# Revit family: Thorn CESAR AMP WALL
name_source: partatom
category: Lighting Fixtures
units: mm (PartAtom-declared; Revit-internal decimal feet)

## family parameters
Cut with Voids When Loaded = Yes
Host = Face
Light Source = No
Maintain Annotation Orientation = No
Part Type = Normal
Room Calculation Point = Yes
Round Connector Dimension = Use Diameter
Shared = No

## types (120) — shared parameters
Assembly Code = Pr_70_70_48_17
Default Elevation = 1000 mm  [stored 3.28084 ft]
Description = Outdoor Wall Mounted Luminaire
Export Type to IFC As = IfcLightFixtureType
Lamp = LED
Manufacturer = Thorn Lighting
Power Factor = 1
R = 36 mm  [stored 0.11811 ft]
Type IFC Predefined Type = DIRECTIONSOURCE
URL = https://www.thornlighting.com

## per-type parameters (varying)
| type | Apparent Load | D | E | Housing L | Housing M | Housing S | Luminaire Height | Luminaire Length | Luminaire Width | Material | Model | Type Image | Type Light Source Down | Type Light Source Up | Up and Down | Wattage |
| CESAR AMP S DWN 1 L927 WB RD WH | 9 VA | 45 mm  [stored 0.147638 ft] | 12 mm  [stored 0.0393701 ft] | No | No | Yes | 250 mm  [stored 0.82021 ft] | 145 mm  [stored 0.475722 ft] | 90 mm  [stored 0.295276 ft] | Thorn-Aluminium-RAL 9016-Traffic White | 96701186 | TLG_CESA_F_AMP_DWN_WB_WH.jpg | Thorn-Light Source-Cesar-Amp-Wall : CESAR AMP S DWN 1 L927 WB RD WH_photometric_data | Thorn-Light Source-Cesar-Amp-Wall : CESAR AMP S DWN 1 L927 WB RD WH_photometric_data | No | 9 W |
| CESAR AMP S DWN 1L927WB HF ANT | 9 VA | 45 mm  [stored 0.147638 ft] | 12 mm  [stored 0.0393701 ft] | No | No | Yes | 250 mm  [stored 0.82021 ft] | 145 mm  [stored 0.475722 ft] | 90 mm  [stored 0.295276 ft] | Thorn-Aluminium-RAL 7016-Anthracite Grey | 96700037 | TLG_CESA_F_AMP_DWN_WB_ANT.jpg | Thorn-Light Source-Cesar-Amp-Wall : CESAR AMP S DWN 1L927WB HF ANT_photometric_data | Thorn-Light Source-Cesar-Amp-Wall : CESAR AMP S DWN 1L927WB HF ANT_photometric_data | No | 9 W |
| CESAR AMP S DWN 1L927WB HF BK | 9 VA | 45 mm  [stored 0.147638 ft] | 12 mm  [stored 0.0393701 ft] | No | No | Yes | 250 mm  [stored 0.82021 ft] | 145 mm  [stored 0.475722 ft] | 90 mm  [stored 0.295276 ft] | Thorn-Aluminium-RAL 9005-Jet Black | 96700035 | TLG_CESA_F_AMP_DWN_WB_BK.jpg | Thorn-Light Source-Cesar-Amp-Wall : CESAR AMP S DWN 1L927WB HF BK_photometric_data | Thorn-Light Source-Cesar-Amp-Wall : CESAR AMP S DWN 1L927WB HF BK_photometric_data | No | 9 W |
| CESAR AMP S DWN 1L927WB HF GY | 9 VA | 45 mm  [stored 0.147638 ft] | 12 mm  [stored 0.0393701 ft] | No | No | Yes | 250 mm  [stored 0.82021 ft] | 145 mm  [stored 0.475722 ft] | 90 mm  [stored 0.295276 ft] | Thorn-Aluminium-RAL 9006-White Aluminium | 96700036 | TLG_CESA_F_AMP_DWN_WB_GY.jpg | Thorn-Light Source-Cesar-Amp-Wall : CESAR AMP S DWN 1L927WB HF GY_photometric_data | Thorn-Light Source-Cesar-Amp-Wall : CESAR AMP S DWN 1L927WB HF GY_photometric_data | No | 9 W |
| CESAR AMP S DWN 1L927WB RD ANT | 9 VA | 45 mm  [stored 0.147638 ft] | 12 mm  [stored 0.0393701 ft] | No | No | Yes | 250 mm  [stored 0.82021 ft] | 145 mm  [stored 0.475722 ft] | 90 mm  [stored 0.295276 ft] | Thorn-Aluminium-RAL 7016-Anthracite Grey | 96701189 | TLG_CESA_F_AMP_DWN_WB_ANT_DarkSkyApproved.jpg | Thorn-Light Source-Cesar-Amp-Wall : CESAR AMP S DWN 1L927WB RD ANT_photometric_data | Thorn-Light Source-Cesar-Amp-Wall : CESAR AMP S DWN 1L927WB RD ANT_photometric_data | No | 9 W |
| CESAR AMP S DWN 1L927WB RD BK | 9 VA | 45 mm  [stored 0.147638 ft] | 12 mm  [stored 0.0393701 ft] | No | No | Yes | 250 mm  [stored 0.82021 ft] | 145 mm  [stored 0.475722 ft] | 90 mm  [stored 0.295276 ft] | Thorn-Aluminium-RAL 9005-Jet Black | 96701187 | TLG_CESA_F_AMP_DWN_WB_BK.jpg | Thorn-Light Source-Cesar-Amp-Wall : CESAR AMP S DWN 1L927WB RD BK_photometric_data | Thorn-Light Source-Cesar-Amp-Wall : CESAR AMP S DWN 1L927WB RD BK_photometric_data | No | 9 W |
| CESAR AMP S DWN 1L927WB RD GY | 9 VA | 45 mm  [stored 0.147638 ft] | 12 mm  [stored 0.0393701 ft] | No | No | Yes | 250 mm  [stored 0.82021 ft] | 145 mm  [stored 0.475722 ft] | 90 mm  [stored 0.295276 ft] | Thorn-Aluminium-RAL 9006-White Aluminium | 96701188 | TLG_CESA_F_AMP_DWN_WB_GY.jpg | Thorn-Light Source-Cesar-Amp-Wall : CESAR AMP S DWN 1L927WB RD GY_photometric_data | Thorn-Light Source-Cesar-Amp-Wall : CESAR AMP S DWN 1L927WB RD GY_photometric_data | No | 9 W |
| CESAR AMP S DWN 1L927WBHF WH | 9 VA | 45 mm  [stored 0.147638 ft] | 12 mm  [stored 0.0393701 ft] | No | No | Yes | 250 mm  [stored 0.82021 ft] | 145 mm  [stored 0.475722 ft] | 90 mm  [stored 0.295276 ft] | Thorn-Aluminium-RAL 9016-Traffic White | 96700034 | TLG_CESA_F_AMP_DWN_WB_WH.jpg | Thorn-Light Source-Cesar-Amp-Wall : CESAR AMP S DWN 1L927WBHF WH_photometric_data | Thorn-Light Source-Cesar-Amp-Wall : CESAR AMP S DWN 1L927WBHF WH_photometric_data | No | 9 W |
| CESAR AMP S DWN 1L930WB HF ANT | 9 VA | 45 mm  [stored 0.147638 ft] | 12 mm  [stored 0.0393701 ft] | No | No | Yes | 250 mm  [stored 0.82021 ft] | 145 mm  [stored 0.475722 ft] | 90 mm  [stored 0.295276 ft] | Thorn-Aluminium-RAL 7016-Anthracite Grey | 96700045 | TLG_CESA_F_AMP_DWN_WB_ANT.jpg | Thorn-Light Source-Cesar-Amp-Wall : CESAR AMP S DWN 1L930WB HF ANT_photometric_data | Thorn-Light Source-Cesar-Amp-Wall : CESAR AMP S DWN 1L930WB HF ANT_photometric_data | No | 9 W |
| CESAR AMP S DWN 1L930WB HF BK | 9 VA | 45 mm  [stored 0.147638 ft] | 12 mm  [stored 0.0393701 ft] | No | No | Yes | 250 mm  [stored 0.82021 ft] | 145 mm  [stored 0.475722 ft] | 90 mm  [stored 0.295276 ft] | Thorn-Aluminium-RAL 9005-Jet Black | 96700043 | TLG_CESA_F_AMP_DWN_WB_BK.jpg | Thorn-Light Source-Cesar-Amp-Wall : CESAR AMP S DWN 1L930WB HF BK_photometric_data | Thorn-Light Source-Cesar-Amp-Wall : CESAR AMP S DWN 1L930WB HF BK_photometric_data | No | 9 W |
| CESAR AMP S DWN 1L930WB HF GY | 9 VA | 45 mm  [stored 0.147638 ft] | 12 mm  [stored 0.0393701 ft] | No | No | Yes | 250 mm  [stored 0.82021 ft] | 145 mm  [stored 0.475722 ft] | 90 mm  [stored 0.295276 ft] | Thorn-Aluminium-RAL 9006-White Aluminium | 96700044 | TLG_CESA_F_AMP_DWN_WB_GY.jpg | Thorn-Light Source-Cesar-Amp-Wall : CESAR AMP S DWN 1L930WB HF GY_photometric_data | Thorn-Light Source-Cesar-Amp-Wall : CESAR AMP S DWN 1L930WB HF GY_photometric_data | No | 9 W |
| CESAR AMP S DWN 1L930WB HF WH | 9 VA | 45 mm  [stored 0.147638 ft] | 12 mm  [stored 0.0393701 ft] | No | No | Yes | 250 mm  [stored 0.82021 ft] | 145 mm  [stored 0.475722 ft] | 90 mm  [stored 0.295276 ft] | Thorn-Aluminium-RAL 9016-Traffic White | 96700042 | TLG_CESA_F_AMP_DWN_WB_WH.jpg | Thorn-Light Source-Cesar-Amp-Wall : CESAR AMP S DWN 1L930WB HF WH_photometric_data | Thorn-Light Source-Cesar-Amp-Wall : CESAR AMP S DWN 1L930WB HF WH_photometric_data | No | 9 W |
| CESAR AMP S DWN 1L930WB RD ANT | 9 VA | 45 mm  [stored 0.147638 ft] | 12 mm  [stored 0.0393701 ft] | No | No | Yes | 250 mm  [stored 0.82021 ft] | 145 mm  [stored 0.475722 ft] | 90 mm  [stored 0.295276 ft] | Thorn-Aluminium-RAL 7016-Anthracite Grey | 96701197 | TLG_CESA_F_AMP_DWN_WB_ANT_DarkSkyApproved.jpg | Thorn-Light Source-Cesar-Amp-Wall : CESAR AMP S DWN 1L930WB RD ANT_photometric_data | Thorn-Light Source-Cesar-Amp-Wall : CESAR AMP S DWN 1L930WB RD ANT_photometric_data | No | 9 W |
| CESAR AMP S DWN 1L930WB RD BK | 9 VA | 45 mm  [stored 0.147638 ft] | 12 mm  [stored 0.0393701 ft] | No | No | Yes | 250 mm  [stored 0.82021 ft] | 145 mm  [stored 0.475722 ft] | 90 mm  [stored 0.295276 ft] | Thorn-Aluminium-RAL 9005-Jet Black | 96701195 | TLG_CESA_F_AMP_DWN_WB_BK.jpg | Thorn-Light Source-Cesar-Amp-Wall : CESAR AMP S DWN 1L930WB RD BK_photometric_data | Thorn-Light Source-Cesar-Amp-Wall : CESAR AMP S DWN 1L930WB RD BK_photometric_data | No | 9 W |
| CESAR AMP S DWN 1L930WB RD GY | 9 VA | 45 mm  [stored 0.147638 ft] | 12 mm  [stored 0.0393701 ft] | No | No | Yes | 250 mm  [stored 0.82021 ft] | 145 mm  [stored 0.475722 ft] | 90 mm  [stored 0.295276 ft] | Thorn-Aluminium-RAL 9006-White Aluminium | 96701196 | TLG_CESA_F_AMP_DWN_WB_GY.jpg | Thorn-Light Source-Cesar-Amp-Wall : CESAR AMP S DWN 1L930WB RD GY_photometric_data | Thorn-Light Source-Cesar-Amp-Wall : CESAR AMP S DWN 1L930WB RD GY_photometric_data | No | 9 W |
| CESAR AMP S DWN 1L930WB RD WH | 9 VA | 45 mm  [stored 0.147638 ft] | 12 mm  [stored 0.0393701 ft] | No | No | Yes | 250 mm  [stored 0.82021 ft] | 145 mm  [stored 0.475722 ft] | 90 mm  [stored 0.295276 ft] | Thorn-Aluminium-RAL 9016-Traffic White | 96701194 | TLG_CESA_F_AMP_DWN_WB_WH.jpg | Thorn-Light Source-Cesar-Amp-Wall : CESAR AMP S DWN 1L930WB RD WH_photometric_data | Thorn-Light Source-Cesar-Amp-Wall : CESAR AMP S DWN 1L930WB RD WH_photometric_data | No | 9 W |
| CESAR AMP S DWN 1L940WB HF ANT | 9 VA | 45 mm  [stored 0.147638 ft] | 12 mm  [stored 0.0393701 ft] | No | No | Yes | 250 mm  [stored 0.82021 ft] | 145 mm  [stored 0.475722 ft] | 90 mm  [stored 0.295276 ft] | Thorn-Aluminium-RAL 7016-Anthracite Grey | 96700041 | TLG_CESA_F_AMP_DWN_WB_ANT.jpg | Thorn-Light Source-Cesar-Amp-Wall : CESAR AMP S DWN 1L940WB HF ANT_photometric_data | Thorn-Light Source-Cesar-Amp-Wall : CESAR AMP S DWN 1L940WB HF ANT_photometric_data | No | 9 W |
| CESAR AMP S DWN 1L940WB HF BK | 9 VA | 45 mm  [stored 0.147638 ft] | 12 mm  [stored 0.0393701 ft] | No | No | Yes | 250 mm  [stored 0.82021 ft] | 145 mm  [stored 0.475722 ft] | 90 mm  [stored 0.295276 ft] | Thorn-Aluminium-RAL 9005-Jet Black | 96700039 | TLG_CESA_F_AMP_DWN_WB_BK.jpg | Thorn-Light Source-Cesar-Amp-Wall : CESAR AMP S DWN 1L940WB HF BK_photometric_data | Thorn-Light Source-Cesar-Amp-Wall : CESAR AMP S DWN 1L940WB HF BK_photometric_data | No | 9 W |
| CESAR AMP S DWN 1L940WB HF GY | 9 VA | 45 mm  [stored 0.147638 ft] | 12 mm  [stored 0.0393701 ft] | No | No | Yes | 250 mm  [stored 0.82021 ft] | 145 mm  [stored 0.475722 ft] | 90 mm  [stored 0.295276 ft] | Thorn-Aluminium-RAL 9006-White Aluminium | 96700040 | TLG_CESA_F_AMP_DWN_WB_GY.jpg | Thorn-Light Source-Cesar-Amp-Wall : CESAR AMP S DWN 1L940WB HF GY_photometric_data | Thorn-Light Source-Cesar-Amp-Wall : CESAR AMP S DWN 1L940WB HF GY_photometric_data | No | 9 W |
| CESAR AMP S DWN 1L940WB HF WH | 9 VA | 45 mm  [stored 0.147638 ft] | 12 mm  [stored 0.0393701 ft] | No | No | Yes | 250 mm  [stored 0.82021 ft] | 145 mm  [stored 0.475722 ft] | 90 mm  [stored 0.295276 ft] | Thorn-Aluminium-RAL 9016-Traffic White | 96700038 | TLG_CESA_F_AMP_DWN_WB_WH.jpg | Thorn-Light Source-Cesar-Amp-Wall : CESAR AMP S DWN 1L940WB HF WH_photometric_data | Thorn-Light Source-Cesar-Amp-Wall : CESAR AMP S DWN 1L940WB HF WH_photometric_data | No | 9 W |
| CESAR AMP S DWN 1L940WB RD ANT | 9 VA | 45 mm  [stored 0.147638 ft] | 12 mm  [stored 0.0393701 ft] | No | No | Yes | 250 mm  [stored 0.82021 ft] | 145 mm  [stored 0.475722 ft] | 90 mm  [stored 0.295276 ft] | Thorn-Aluminium-RAL 7016-Anthracite Grey | 96701193 | TLG_CESA_F_AMP_DWN_WB_ANT.jpg | Thorn-Light Source-Cesar-Amp-Wall : CESAR AMP S DWN 1L940WB RD ANT_photometric_data | Thorn-Light Source-Cesar-Amp-Wall : CESAR AMP S DWN 1L940WB RD ANT_photometric_data | No | 9 W |
| CESAR AMP S DWN 1L940WB RD BK | 9 VA | 45 mm  [stored 0.147638 ft] | 12 mm  [stored 0.0393701 ft] | No | No | Yes | 250 mm  [stored 0.82021 ft] | 145 mm  [stored 0.475722 ft] | 90 mm  [stored 0.295276 ft] | Thorn-Aluminium-RAL 9005-Jet Black | 96701191 | TLG_CESA_F_AMP_DWN_WB_BK.jpg | Thorn-Light Source-Cesar-Amp-Wall : CESAR AMP S DWN 1L940WB RD BK_photometric_data | Thorn-Light Source-Cesar-Amp-Wall : CESAR AMP S DWN 1L940WB RD BK_photometric_data | No | 9 W |
| CESAR AMP S DWN 1L940WB RD GY | 9 VA | 45 mm  [stored 0.147638 ft] | 12 mm  [stored 0.0393701 ft] | No | No | Yes | 250 mm  [stored 0.82021 ft] | 145 mm  [stored 0.475722 ft] | 90 mm  [stored 0.295276 ft] | Thorn-Aluminium-RAL 9006-White Aluminium | 96701192 | TLG_CESA_F_AMP_DWN_WB_GY.jpg | Thorn-Light Source-Cesar-Amp-Wall : CESAR AMP S DWN 1L940WB RD GY_photometric_data | Thorn-Light Source-Cesar-Amp-Wall : CESAR AMP S DWN 1L940WB RD GY_photometric_data | No | 9 W |
| CESAR AMP S DWN 1L940WB RD WH | 9 VA | 45 mm  [stored 0.147638 ft] | 12 mm  [stored 0.0393701 ft] | No | No | Yes | 250 mm  [stored 0.82021 ft] | 145 mm  [stored 0.475722 ft] | 90 mm  [stored 0.295276 ft] | Thorn-Aluminium-RAL 9016-Traffic White | 96701190 | TLG_CESA_F_AMP_DWN_WB_WH.jpg | Thorn-Light Source-Cesar-Amp-Wall : CESAR AMP S DWN 1L940WB RD WH_photometric_data | Thorn-Light Source-Cesar-Amp-Wall : CESAR AMP S DWN 1L940WB RD WH_photometric_data | No | 9 W |
| CESAR AMP S U/D 2L927WB HF ANT | 15 VA | 45 mm  [stored 0.147638 ft] | 12 mm  [stored 0.0393701 ft] | No | No | Yes | 250 mm  [stored 0.82021 ft] | 145 mm  [stored 0.475722 ft] | 90 mm  [stored 0.295276 ft] | Thorn-Aluminium-RAL 7016-Anthracite Grey | 96700049 | TLG_CESA_F_AMP_UD_WB_ANT.jpg | Thorn-Light Source-Cesar-Amp-Wall : CESAR AMP S U/D 2L927WB HF ANT_photometric_data_DOWN | Thorn-Light Source-Cesar-Amp-Wall : CESAR AMP S U/D 2L927WB HF ANT_photometric_data_UP | Yes | 15 W |
| CESAR AMP S U/D 2L927WB HF BK | 15 VA | 45 mm  [stored 0.147638 ft] | 12 mm  [stored 0.0393701 ft] | No | No | Yes | 250 mm  [stored 0.82021 ft] | 145 mm  [stored 0.475722 ft] | 90 mm  [stored 0.295276 ft] | Thorn-Aluminium-RAL 9005-Jet Black | 96700047 | TLG_CESA_F_AMP_UD_WB_BK.jpg | Thorn-Light Source-Cesar-Amp-Wall : CESAR AMP S U/D 2L927WB HF BK_photometric_data_DOWN | Thorn-Light Source-Cesar-Amp-Wall : CESAR AMP S U/D 2L927WB HF BK_photometric_data_UP | Yes | 15 W |
| CESAR AMP S U/D 2L927WB HF GY | 15 VA | 45 mm  [stored 0.147638 ft] | 12 mm  [stored 0.0393701 ft] | No | No | Yes | 250 mm  [stored 0.82021 ft] | 145 mm  [stored 0.475722 ft] | 90 mm  [stored 0.295276 ft] | Thorn-Aluminium-RAL 9006-White Aluminium | 96700048 | TLG_CESA_F_AMP_UD_WB_GY.jpg | Thorn-Light Source-Cesar-Amp-Wall : CESAR AMP S U/D 2L927WB HF GY_photometric_data_DOWN | Thorn-Light Source-Cesar-Amp-Wall : CESAR AMP S U/D 2L927WB HF GY_photometric_data_UP | Yes | 15 W |
| CESAR AMP S U/D 2L927WB HF WH | 15 VA | 45 mm  [stored 0.147638 ft] | 12 mm  [stored 0.0393701 ft] | No | No | Yes | 250 mm  [stored 0.82021 ft] | 145 mm  [stored 0.475722 ft] | 90 mm  [stored 0.295276 ft] | Thorn-Aluminium-RAL 9016-Traffic White | 96700046 | TLG_CESA_F_AMP_UD_WB_WH.jpg | Thorn-Light Source-Cesar-Amp-Wall : CESAR AMP S U/D 2L927WB HF WH_photometric_data_DOWN | Thorn-Light Source-Cesar-Amp-Wall : CESAR AMP S U/D 2L927WB HF WH_photometric_data_UP | Yes | 15 W |
| CESAR AMP S U/D 2L927WB RD ANT | 15 VA | 45 mm  [stored 0.147638 ft] | 12 mm  [stored 0.0393701 ft] | No | No | Yes | 250 mm  [stored 0.82021 ft] | 145 mm  [stored 0.475722 ft] | 90 mm  [stored 0.295276 ft] | Thorn-Aluminium-RAL 7016-Anthracite Grey | 96701201 | TLG_CESA_F_AMP_UD_WB_ANT.jpg | Thorn-Light Source-Cesar-Amp-Wall : CESAR AMP S U/D 2L927WB RD ANT_photometric_data_DOWN | Thorn-Light Source-Cesar-Amp-Wall : CESAR AMP S U/D 2L927WB RD ANT_photometric_data_UP | Yes | 15 W |
| CESAR AMP S U/D 2L927WB RD BK | 15 VA | 45 mm  [stored 0.147638 ft] | 12 mm  [stored 0.0393701 ft] | No | No | Yes | 250 mm  [stored 0.82021 ft] | 145 mm  [stored 0.475722 ft] | 90 mm  [stored 0.295276 ft] | Thorn-Aluminium-RAL 9005-Jet Black | 96701199 | TLG_CESA_F_AMP_UD_WB_BK.jpg | Thorn-Light Source-Cesar-Amp-Wall : CESAR AMP S U/D 2L927WB RD BK_photometric_data_DOWN | Thorn-Light Source-Cesar-Amp-Wall : CESAR AMP S U/D 2L927WB RD BK_photometric_data_UP | Yes | 15 W |
| CESAR AMP S U/D 2L927WB RD GY | 15 VA | 45 mm  [stored 0.147638 ft] | 12 mm  [stored 0.0393701 ft] | No | No | Yes | 250 mm  [stored 0.82021 ft] | 145 mm  [stored 0.475722 ft] | 90 mm  [stored 0.295276 ft] | Thorn-Aluminium-RAL 9006-White Aluminium | 96701200 | TLG_CESA_F_AMP_UD_WB_GY.jpg | Thorn-Light Source-Cesar-Amp-Wall : CESAR AMP S U/D 2L927WB RD GY_photometric_data_DOWN | Thorn-Light Source-Cesar-Amp-Wall : CESAR AMP S U/D 2L927WB RD GY_photometric_data_UP | Yes | 15 W |
| CESAR AMP S U/D 2L927WB RD WH | 15 VA | 45 mm  [stored 0.147638 ft] | 12 mm  [stored 0.0393701 ft] | No | No | Yes | 250 mm  [stored 0.82021 ft] | 145 mm  [stored 0.475722 ft] | 90 mm  [stored 0.295276 ft] | Thorn-Aluminium-RAL 9016-Traffic White | 96701198 | TLG_CESA_F_AMP_UD_WB_WH.jpg | Thorn-Light Source-Cesar-Amp-Wall : CESAR AMP S U/D 2L927WB RD WH_photometric_data_DOWN | Thorn-Light Source-Cesar-Amp-Wall : CESAR AMP S U/D 2L927WB RD WH_photometric_data_UP | Yes | 15 W |
| CESAR AMP S U/D 2L930WB HF ANT | 15 VA | 45 mm  [stored 0.147638 ft] | 12 mm  [stored 0.0393701 ft] | No | No | Yes | 250 mm  [stored 0.82021 ft] | 145 mm  [stored 0.475722 ft] | 90 mm  [stored 0.295276 ft] | Thorn-Aluminium-RAL 7016-Anthracite Grey | 96700057 | TLG_CESA_F_AMP_UD_WB_ANT.jpg | Thorn-Light Source-Cesar-Amp-Wall : CESAR AMP S U/D 2L930WB HF ANT_photometric_data_DOWN | Thorn-Light Source-Cesar-Amp-Wall : CESAR AMP S U/D 2L930WB HF ANT_photometric_data_UP | Yes | 15 W |
| CESAR AMP S U/D 2L930WB HF BK | 15 VA | 45 mm  [stored 0.147638 ft] | 12 mm  [stored 0.0393701 ft] | No | No | Yes | 250 mm  [stored 0.82021 ft] | 145 mm  [stored 0.475722 ft] | 90 mm  [stored 0.295276 ft] | Thorn-Aluminium-RAL 9005-Jet Black | 96700055 | TLG_CESA_F_AMP_UD_WB_BK.jpg | Thorn-Light Source-Cesar-Amp-Wall : CESAR AMP S U/D 2L930WB HF BK_photometric_data_DOWN | Thorn-Light Source-Cesar-Amp-Wall : CESAR AMP S U/D 2L930WB HF BK_photometric_data_UP | Yes | 15 W |
| CESAR AMP S U/D 2L930WB HF GY | 15 VA | 45 mm  [stored 0.147638 ft] | 12 mm  [stored 0.0393701 ft] | No | No | Yes | 250 mm  [stored 0.82021 ft] | 145 mm  [stored 0.475722 ft] | 90 mm  [stored 0.295276 ft] | Thorn-Aluminium-RAL 9006-White Aluminium | 96700056 | TLG_CESA_F_AMP_UD_WB_GY.jpg | Thorn-Light Source-Cesar-Amp-Wall : CESAR AMP S U/D 2L930WB HF GY_photometric_data_DOWN | Thorn-Light Source-Cesar-Amp-Wall : CESAR AMP S U/D 2L930WB HF GY_photometric_data_UP | Yes | 15 W |
| CESAR AMP S U/D 2L930WB HF WH | 15 VA | 45 mm  [stored 0.147638 ft] | 12 mm  [stored 0.0393701 ft] | No | No | Yes | 250 mm  [stored 0.82021 ft] | 145 mm  [stored 0.475722 ft] | 90 mm  [stored 0.295276 ft] | Thorn-Aluminium-RAL 9016-Traffic White | 96700054 | TLG_CESA_F_AMP_UD_WB_WH.jpg | Thorn-Light Source-Cesar-Amp-Wall : CESAR AMP S U/D 2L930WB HF WH_photometric_data_DOWN | Thorn-Light Source-Cesar-Amp-Wall : CESAR AMP S U/D 2L930WB HF WH_photometric_data_UP | Yes | 15 W |
| CESAR AMP S U/D 2L930WB RD ANT | 15 VA | 45 mm  [stored 0.147638 ft] | 12 mm  [stored 0.0393701 ft] | No | No | Yes | 250 mm  [stored 0.82021 ft] | 145 mm  [stored 0.475722 ft] | 90 mm  [stored 0.295276 ft] | Thorn-Aluminium-RAL 7016-Anthracite Grey | 96701209 | TLG_CESA_F_AMP_UD_WB_ANT.jpg | Thorn-Light Source-Cesar-Amp-Wall : CESAR AMP S U/D 2L930WB RD ANT_photometric_data_DOWN | Thorn-Light Source-Cesar-Amp-Wall : CESAR AMP S U/D 2L930WB RD ANT_photometric_data_UP | Yes | 15 W |
| CESAR AMP S U/D 2L930WB RD BK | 15 VA | 45 mm  [stored 0.147638 ft] | 12 mm  [stored 0.0393701 ft] | No | No | Yes | 250 mm  [stored 0.82021 ft] | 145 mm  [stored 0.475722 ft] | 90 mm  [stored 0.295276 ft] | Thorn-Aluminium-RAL 9005-Jet Black | 96701207 | TLG_CESA_F_AMP_UD_WB_BK.jpg | Thorn-Light Source-Cesar-Amp-Wall : CESAR AMP S U/D 2L930WB RD BK_photometric_data_DOWN | Thorn-Light Source-Cesar-Amp-Wall : CESAR AMP S U/D 2L930WB RD BK_photometric_data_UP | Yes | 15 W |
| CESAR AMP S U/D 2L930WB RD GY | 15 VA | 45 mm  [stored 0.147638 ft] | 12 mm  [stored 0.0393701 ft] | No | No | Yes | 250 mm  [stored 0.82021 ft] | 145 mm  [stored 0.475722 ft] | 90 mm  [stored 0.295276 ft] | Thorn-Aluminium-RAL 9006-White Aluminium | 96701208 | TLG_CESA_F_AMP_UD_WB_GY.jpg | Thorn-Light Source-Cesar-Amp-Wall : CESAR AMP S U/D 2L930WB RD GY_photometric_data_DOWN | Thorn-Light Source-Cesar-Amp-Wall : CESAR AMP S U/D 2L930WB RD GY_photometric_data_UP | Yes | 15 W |
| CESAR AMP S U/D 2L930WB RD WH | 15 VA | 45 mm  [stored 0.147638 ft] | 12 mm  [stored 0.0393701 ft] | No | No | Yes | 250 mm  [stored 0.82021 ft] | 145 mm  [stored 0.475722 ft] | 90 mm  [stored 0.295276 ft] | Thorn-Aluminium-RAL 9016-Traffic White | 96701206 | TLG_CESA_F_AMP_UD_WB_WH.jpg | Thorn-Light Source-Cesar-Amp-Wall : CESAR AMP S U/D 2L930WB RD WH_photometric_data_DOWN | Thorn-Light Source-Cesar-Amp-Wall : CESAR AMP S U/D 2L930WB RD WH_photometric_data_UP | Yes | 15 W |
| CESAR AMP S U/D 2L940WB HF ANT | 15 VA | 45 mm  [stored 0.147638 ft] | 12 mm  [stored 0.0393701 ft] | No | No | Yes | 250 mm  [stored 0.82021 ft] | 145 mm  [stored 0.475722 ft] | 90 mm  [stored 0.295276 ft] | Thorn-Aluminium-RAL 7016-Anthracite Grey | 96700053 | TLG_CESA_F_AMP_UD_WB_ANT.jpg | Thorn-Light Source-Cesar-Amp-Wall : CESAR AMP S U/D 2L940WB HF ANT_photometric_data_DOWN | Thorn-Light Source-Cesar-Amp-Wall : CESAR AMP S U/D 2L940WB HF ANT_photometric_data_UP | Yes | 15 W |
| CESAR AMP S U/D 2L940WB HF BK | 15 VA | 45 mm  [stored 0.147638 ft] | 12 mm  [stored 0.0393701 ft] | No | No | Yes | 250 mm  [stored 0.82021 ft] | 145 mm  [stored 0.475722 ft] | 90 mm  [stored 0.295276 ft] | Thorn-Aluminium-RAL 9005-Jet Black | 96700051 | TLG_CESA_F_AMP_UD_WB_BK.jpg | Thorn-Light Source-Cesar-Amp-Wall : CESAR AMP S U/D 2L940WB HF BK_photometric_data_DOWN | Thorn-Light Source-Cesar-Amp-Wall : CESAR AMP S U/D 2L940WB HF BK_photometric_data_UP | Yes | 15 W |
| CESAR AMP S U/D 2L940WB HF GY | 15 VA | 45 mm  [stored 0.147638 ft] | 12 mm  [stored 0.0393701 ft] | No | No | Yes | 250 mm  [stored 0.82021 ft] | 145 mm  [stored 0.475722 ft] | 90 mm  [stored 0.295276 ft] | Thorn-Aluminium-RAL 9006-White Aluminium | 96700052 | TLG_CESA_F_AMP_UD_WB_GY.jpg | Thorn-Light Source-Cesar-Amp-Wall : CESAR AMP S U/D 2L940WB HF GY_photometric_data_DOWN | Thorn-Light Source-Cesar-Amp-Wall : CESAR AMP S U/D 2L940WB HF GY_photometric_data_UP | Yes | 15 W |
| CESAR AMP S U/D 2L940WB HF WH | 15 VA | 45 mm  [stored 0.147638 ft] | 12 mm  [stored 0.0393701 ft] | No | No | Yes | 250 mm  [stored 0.82021 ft] | 145 mm  [stored 0.475722 ft] | 90 mm  [stored 0.295276 ft] | Thorn-Aluminium-RAL 9016-Traffic White | 96700050 | TLG_CESA_F_AMP_UD_WB_WH.jpg | Thorn-Light Source-Cesar-Amp-Wall : CESAR AMP S U/D 2L940WB HF WH_photometric_data_DOWN | Thorn-Light Source-Cesar-Amp-Wall : CESAR AMP S U/D 2L940WB HF WH_photometric_data_UP | Yes | 15 W |
| CESAR AMP S U/D 2L940WB RD ANT | 15 VA | 45 mm  [stored 0.147638 ft] | 12 mm  [stored 0.0393701 ft] | No | No | Yes | 250 mm  [stored 0.82021 ft] | 145 mm  [stored 0.475722 ft] | 90 mm  [stored 0.295276 ft] | Thorn-Aluminium-RAL 7016-Anthracite Grey | 96701205 | TLG_CESA_F_AMP_UD_WB_ANT.jpg | Thorn-Light Source-Cesar-Amp-Wall : CESAR AMP S U/D 2L940WB RD ANT_photometric_data_DOWN | Thorn-Light Source-Cesar-Amp-Wall : CESAR AMP S U/D 2L940WB RD ANT_photometric_data_UP | Yes | 15 W |
| CESAR AMP S U/D 2L940WB RD BK | 15 VA | 45 mm  [stored 0.147638 ft] | 12 mm  [stored 0.0393701 ft] | No | No | Yes | 250 mm  [stored 0.82021 ft] | 145 mm  [stored 0.475722 ft] | 90 mm  [stored 0.295276 ft] | Thorn-Aluminium-RAL 9005-Jet Black | 96701203 | TLG_CESA_F_AMP_UD_WB_BK.jpg | Thorn-Light Source-Cesar-Amp-Wall : CESAR AMP S U/D 2L940WB RD BK_photometric_data_DOWN | Thorn-Light Source-Cesar-Amp-Wall : CESAR AMP S U/D 2L940WB RD BK_photometric_data_UP | Yes | 15 W |
| CESAR AMP S U/D 2L940WB RD GY | 15 VA | 45 mm  [stored 0.147638 ft] | 12 mm  [stored 0.0393701 ft] | No | No | Yes | 250 mm  [stored 0.82021 ft] | 145 mm  [stored 0.475722 ft] | 90 mm  [stored 0.295276 ft] | Thorn-Aluminium-RAL 9006-White Aluminium | 96701204 | TLG_CESA_F_AMP_UD_WB_GY.jpg | Thorn-Light Source-Cesar-Amp-Wall : CESAR AMP S U/D 2L940WB RD GY_photometric_data_DOWN | Thorn-Light Source-Cesar-Amp-Wall : CESAR AMP S U/D 2L940WB RD GY_photometric_data_UP | Yes | 15 W |
| CESAR AMP S U/D 2L940WB RD WH | 15 VA | 45 mm  [stored 0.147638 ft] | 12 mm  [stored 0.0393701 ft] | No | No | Yes | 250 mm  [stored 0.82021 ft] | 145 mm  [stored 0.475722 ft] | 90 mm  [stored 0.295276 ft] | Thorn-Aluminium-RAL 9016-Traffic White | 96701202 | TLG_CESA_F_AMP_UD_WB_WH.jpg | Thorn-Light Source-Cesar-Amp-Wall : CESAR AMP S U/D 2L940WB RD WH_photometric_data_DOWN | Thorn-Light Source-Cesar-Amp-Wall : CESAR AMP S U/D 2L940WB RD WH_photometric_data_UP | Yes | 15 W |
| CESAR AMP M DWN 1L927MB HF ANT | 19 VA | 70 mm  [stored 0.229659 ft] | 17 mm | No | Yes | No | 350 mm  [stored 1.14829 ft] | 210 mm  [stored 0.688976 ft] | 140 mm  [stored 0.459318 ft] | Thorn-Aluminium-RAL 7016-Anthracite Grey | 96700073 | TLG_CESA_F_AMP_DWN_WB_ANT.jpg | Thorn-Light Source-Cesar-Amp-Wall : CESAR AMP M DWN 1L927MB HF ANT_photometric_data | Thorn-Light Source-Cesar-Amp-Wall : CESAR AMP M DWN 1L927MB HF ANT_photometric_data | No | 19 W |
| CESAR AMP M DWN 1L927MB HF BK | 19 VA | 70 mm  [stored 0.229659 ft] | 17 mm | No | Yes | No | 350 mm  [stored 1.14829 ft] | 210 mm  [stored 0.688976 ft] | 140 mm  [stored 0.459318 ft] | Thorn-Aluminium-RAL 9005-Jet Black | 96700071 | TLG_CESA_F_AMP_DWN_WB_BK.jpg | Thorn-Light Source-Cesar-Amp-Wall : CESAR AMP M DWN 1L927MB HF BK_photometric_data | Thorn-Light Source-Cesar-Amp-Wall : CESAR AMP M DWN 1L927MB HF BK_photometric_data | No | 19 W |
| CESAR AMP M DWN 1L927MB HF GY | 19 VA | 70 mm  [stored 0.229659 ft] | 17 mm | No | Yes | No | 350 mm  [stored 1.14829 ft] | 210 mm  [stored 0.688976 ft] | 140 mm  [stored 0.459318 ft] | Thorn-Aluminium-RAL 9006-White Aluminium | 96700072 | TLG_CESA_F_AMP_DWN_WB_GY.jpg | Thorn-Light Source-Cesar-Amp-Wall : CESAR AMP M DWN 1L927MB HF GY_photometric_data | Thorn-Light Source-Cesar-Amp-Wall : CESAR AMP M DWN 1L927MB HF GY_photometric_data | No | 19 W |
| CESAR AMP M DWN 1L927MB HF WH | 19 VA | 70 mm  [stored 0.229659 ft] | 17 mm | No | Yes | No | 350 mm  [stored 1.14829 ft] | 210 mm  [stored 0.688976 ft] | 140 mm  [stored 0.459318 ft] | Thorn-Aluminium-RAL 9016-Traffic White | 96700070 | TLG_CESA_F_AMP_DWN_WB_WH.jpg | Thorn-Light Source-Cesar-Amp-Wall : CESAR AMP M DWN 1L927MB HF WH_photometric_data | Thorn-Light Source-Cesar-Amp-Wall : CESAR AMP M DWN 1L927MB HF WH_photometric_data | No | 19 W |
| CESAR AMP M DWN 1L927MB RD ANT | 19 VA | 70 mm  [stored 0.229659 ft] | 17 mm | No | Yes | No | 350 mm  [stored 1.14829 ft] | 210 mm  [stored 0.688976 ft] | 140 mm  [stored 0.459318 ft] | Thorn-Aluminium-RAL 7016-Anthracite Grey | 96701225 | TLG_CESA_F_AMP_DWN_WB_ANT_DarkSkyApproved.jpg | Thorn-Light Source-Cesar-Amp-Wall : CESAR AMP M DWN 1L927MB RD ANT_photometric_data | Thorn-Light Source-Cesar-Amp-Wall : CESAR AMP M DWN 1L927MB RD ANT_photometric_data | No | 19 W |
| CESAR AMP M DWN 1L927MB RD BK | 19 VA | 70 mm  [stored 0.229659 ft] | 17 mm | No | Yes | No | 350 mm  [stored 1.14829 ft] | 210 mm  [stored 0.688976 ft] | 140 mm  [stored 0.459318 ft] | Thorn-Aluminium-RAL 9005-Jet Black | 96701223 | TLG_CESA_F_AMP_DWN_WB_BK.jpg | Thorn-Light Source-Cesar-Amp-Wall : CESAR AMP M DWN 1L927MB RD BK_photometric_data | Thorn-Light Source-Cesar-Amp-Wall : CESAR AMP M DWN 1L927MB RD BK_photometric_data | No | 19 W |
| CESAR AMP M DWN 1L927MB RD GY | 19 VA | 70 mm  [stored 0.229659 ft] | 17 mm | No | Yes | No | 350 mm  [stored 1.14829 ft] | 210 mm  [stored 0.688976 ft] | 140 mm  [stored 0.459318 ft] | Thorn-Aluminium-RAL 9006-White Aluminium | 96701224 | TLG_CESA_F_AMP_DWN_WB_GY.jpg | Thorn-Light Source-Cesar-Amp-Wall : CESAR AMP M DWN 1L927MB RD GY_photometric_data | Thorn-Light Source-Cesar-Amp-Wall : CESAR AMP M DWN 1L927MB RD GY_photometric_data | No | 19 W |
| CESAR AMP M DWN 1L927MB RD WH | 19 VA | 70 mm  [stored 0.229659 ft] | 17 mm | No | Yes | No | 350 mm  [stored 1.14829 ft] | 210 mm  [stored 0.688976 ft] | 140 mm  [stored 0.459318 ft] | Thorn-Aluminium-RAL 9016-Traffic White | 96701222 | TLG_CESA_F_AMP_DWN_WB_WH.jpg | Thorn-Light Source-Cesar-Amp-Wall : CESAR AMP M DWN 1L927MB RD WH_photometric_data | Thorn-Light Source-Cesar-Amp-Wall : CESAR AMP M DWN 1L927MB RD WH_photometric_data | No | 19 W |
| CESAR AMP M DWN 1L930MB HF ANT | 19 VA | 70 mm  [stored 0.229659 ft] | 17 mm | No | Yes | No | 350 mm  [stored 1.14829 ft] | 210 mm  [stored 0.688976 ft] | 140 mm  [stored 0.459318 ft] | Thorn-Aluminium-RAL 7016-Anthracite Grey | 96700081 | TLG_CESA_F_AMP_DWN_WB_ANT.jpg | Thorn-Light Source-Cesar-Amp-Wall : CESAR AMP M DWN 1L930MB HF ANT_photometric_data | Thorn-Light Source-Cesar-Amp-Wall : CESAR AMP M DWN 1L930MB HF ANT_photometric_data | No | 19 W |
| CESAR AMP M DWN 1L930MB HF BK | 19 VA | 70 mm  [stored 0.229659 ft] | 17 mm | No | Yes | No | 350 mm  [stored 1.14829 ft] | 210 mm  [stored 0.688976 ft] | 140 mm  [stored 0.459318 ft] | Thorn-Aluminium-RAL 9005-Jet Black | 96700079 | TLG_CESA_F_AMP_DWN_WB_BK.jpg | Thorn-Light Source-Cesar-Amp-Wall : CESAR AMP M DWN 1L930MB HF BK_photometric_data | Thorn-Light Source-Cesar-Amp-Wall : CESAR AMP M DWN 1L930MB HF BK_photometric_data | No | 19 W |
| CESAR AMP M DWN 1L930MB HF GY | 19 VA | 70 mm  [stored 0.229659 ft] | 17 mm | No | Yes | No | 350 mm  [stored 1.14829 ft] | 210 mm  [stored 0.688976 ft] | 140 mm  [stored 0.459318 ft] | Thorn-Aluminium-RAL 9006-White Aluminium | 96700080 | TLG_CESA_F_AMP_DWN_WB_GY.jpg | Thorn-Light Source-Cesar-Amp-Wall : CESAR AMP M DWN 1L930MB HF GY_photometric_data | Thorn-Light Source-Cesar-Amp-Wall : CESAR AMP M DWN 1L930MB HF GY_photometric_data | No | 19 W |
| CESAR AMP M DWN 1L930MB HF WH | 19 VA | 70 mm  [stored 0.229659 ft] | 17 mm | No | Yes | No | 350 mm  [stored 1.14829 ft] | 210 mm  [stored 0.688976 ft] | 140 mm  [stored 0.459318 ft] | Thorn-Aluminium-RAL 9016-Traffic White | 96700078 | TLG_CESA_F_AMP_DWN_WB_WH.jpg | Thorn-Light Source-Cesar-Amp-Wall : CESAR AMP M DWN 1L930MB HF WH_photometric_data | Thorn-Light Source-Cesar-Amp-Wall : CESAR AMP M DWN 1L930MB HF WH_photometric_data | No | 19 W |
| CESAR AMP M DWN 1L930MB RD ANT | 19 VA | 70 mm  [stored 0.229659 ft] | 17 mm | No | Yes | No | 350 mm  [stored 1.14829 ft] | 210 mm  [stored 0.688976 ft] | 140 mm  [stored 0.459318 ft] | Thorn-Aluminium-RAL 7016-Anthracite Grey | 96701233 | TLG_CESA_F_AMP_DWN_WB_ANT.jpg | Thorn-Light Source-Cesar-Amp-Wall : CESAR AMP M DWN 1L930MB RD ANT_photometric_data | Thorn-Light Source-Cesar-Amp-Wall : CESAR AMP M DWN 1L930MB RD ANT_photometric_data | No | 19 W |
| CESAR AMP M DWN 1L930MB RD BK | 19 VA | 70 mm  [stored 0.229659 ft] | 17 mm | No | Yes | No | 350 mm  [stored 1.14829 ft] | 210 mm  [stored 0.688976 ft] | 140 mm  [stored 0.459318 ft] | Thorn-Aluminium-RAL 9005-Jet Black | 96701231 | TLG_CESA_F_AMP_DWN_WB_BK.jpg | Thorn-Light Source-Cesar-Amp-Wall : CESAR AMP M DWN 1L930MB RD BK_photometric_data | Thorn-Light Source-Cesar-Amp-Wall : CESAR AMP M DWN 1L930MB RD BK_photometric_data | No | 19 W |
| CESAR AMP M DWN 1L930MB RD GY | 19 VA | 70 mm  [stored 0.229659 ft] | 17 mm | No | Yes | No | 350 mm  [stored 1.14829 ft] | 210 mm  [stored 0.688976 ft] | 140 mm  [stored 0.459318 ft] | Thorn-Aluminium-RAL 9006-White Aluminium | 96701232 | TLG_CESA_F_AMP_DWN_WB_GY.jpg | Thorn-Light Source-Cesar-Amp-Wall : CESAR AMP M DWN 1L930MB RD GY_photometric_data | Thorn-Light Source-Cesar-Amp-Wall : CESAR AMP M DWN 1L930MB RD GY_photometric_data | No | 19 W |
| CESAR AMP M DWN 1L930MB RD WH | 19 VA | 70 mm  [stored 0.229659 ft] | 17 mm | No | Yes | No | 350 mm  [stored 1.14829 ft] | 210 mm  [stored 0.688976 ft] | 140 mm  [stored 0.459318 ft] | Thorn-Aluminium-RAL 9016-Traffic White | 96701230 | TLG_CESA_F_AMP_DWN_WB_WH.jpg | Thorn-Light Source-Cesar-Amp-Wall : CESAR AMP M DWN 1L930MB RD WH_photometric_data | Thorn-Light Source-Cesar-Amp-Wall : CESAR AMP M DWN 1L930MB RD WH_photometric_data | No | 19 W |
| CESAR AMP M DWN 1L940MB HF ANT | 19 VA | 70 mm  [stored 0.229659 ft] | 17 mm | No | Yes | No | 350 mm  [stored 1.14829 ft] | 210 mm  [stored 0.688976 ft] | 140 mm  [stored 0.459318 ft] | Thorn-Aluminium-RAL 7016-Anthracite Grey | 96700077 | TLG_CESA_F_AMP_DWN_WB_ANT.jpg | Thorn-Light Source-Cesar-Amp-Wall : CESAR AMP M DWN 1L940MB HF ANT_photometric_data | Thorn-Light Source-Cesar-Amp-Wall : CESAR AMP M DWN 1L940MB HF ANT_photometric_data | No | 19 W |
| CESAR AMP M DWN 1L940MB HF BK | 19 VA | 70 mm  [stored 0.229659 ft] | 17 mm | No | Yes | No | 350 mm  [stored 1.14829 ft] | 210 mm  [stored 0.688976 ft] | 140 mm  [stored 0.459318 ft] | Thorn-Aluminium-RAL 9005-Jet Black | 96700075 | TLG_CESA_F_AMP_DWN_WB_BK.jpg | Thorn-Light Source-Cesar-Amp-Wall : CESAR AMP M DWN 1L940MB HF BK_photometric_data | Thorn-Light Source-Cesar-Amp-Wall : CESAR AMP M DWN 1L940MB HF BK_photometric_data | No | 19 W |
| CESAR AMP M DWN 1L940MB HF GY | 19 VA | 70 mm  [stored 0.229659 ft] | 17 mm | No | Yes | No | 350 mm  [stored 1.14829 ft] | 210 mm  [stored 0.688976 ft] | 140 mm  [stored 0.459318 ft] | Thorn-Aluminium-RAL 9006-White Aluminium | 96700076 | TLG_CESA_F_AMP_DWN_WB_GY.jpg | Thorn-Light Source-Cesar-Amp-Wall : CESAR AMP M DWN 1L940MB HF GY_photometric_data | Thorn-Light Source-Cesar-Amp-Wall : CESAR AMP M DWN 1L940MB HF GY_photometric_data | No | 19 W |
| CESAR AMP M DWN 1L940MB HF WH | 19 VA | 70 mm  [stored 0.229659 ft] | 17 mm | No | Yes | No | 350 mm  [stored 1.14829 ft] | 210 mm  [stored 0.688976 ft] | 140 mm  [stored 0.459318 ft] | Thorn-Aluminium-RAL 9016-Traffic White | 96700074 | TLG_CESA_F_AMP_DWN_WB_WH.jpg | Thorn-Light Source-Cesar-Amp-Wall : CESAR AMP M DWN 1L940MB HF WH_photometric_data | Thorn-Light Source-Cesar-Amp-Wall : CESAR AMP M DWN 1L940MB HF WH_photometric_data | No | 19 W |
| CESAR AMP M DWN 1L940MB RD ANT | 19 VA | 70 mm  [stored 0.229659 ft] | 17 mm | No | Yes | No | 350 mm  [stored 1.14829 ft] | 210 mm  [stored 0.688976 ft] | 140 mm  [stored 0.459318 ft] | Thorn-Aluminium-RAL 7016-Anthracite Grey | 96701229 | TLG_CESA_F_AMP_DWN_WB_ANT.jpg | Thorn-Light Source-Cesar-Amp-Wall : CESAR AMP M DWN 1L940MB RD ANT_photometric_data | Thorn-Light Source-Cesar-Amp-Wall : CESAR AMP M DWN 1L940MB RD ANT_photometric_data | No | 19 W |
| CESAR AMP M DWN 1L940MB RD BK | 19 VA | 70 mm  [stored 0.229659 ft] | 17 mm | No | Yes | No | 350 mm  [stored 1.14829 ft] | 210 mm  [stored 0.688976 ft] | 140 mm  [stored 0.459318 ft] | Thorn-Aluminium-RAL 9005-Jet Black | 96701227 | TLG_CESA_F_AMP_DWN_WB_BK.jpg | Thorn-Light Source-Cesar-Amp-Wall : CESAR AMP M DWN 1L940MB RD BK_photometric_data | Thorn-Light Source-Cesar-Amp-Wall : CESAR AMP M DWN 1L940MB RD BK_photometric_data | No | 19 W |
| CESAR AMP M DWN 1L940MB RD GY | 19 VA | 70 mm  [stored 0.229659 ft] | 17 mm | No | Yes | No | 350 mm  [stored 1.14829 ft] | 210 mm  [stored 0.688976 ft] | 140 mm  [stored 0.459318 ft] | Thorn-Aluminium-RAL 9006-White Aluminium | 96701228 | TLG_CESA_F_AMP_DWN_WB_GY.jpg | Thorn-Light Source-Cesar-Amp-Wall : CESAR AMP M DWN 1L940MB RD GY_photometric_data | Thorn-Light Source-Cesar-Amp-Wall : CESAR AMP M DWN 1L940MB RD GY_photometric_data | No | 19 W |
| CESAR AMP M DWN 1L940MB RD WH | 19 VA | 70 mm  [stored 0.229659 ft] | 17 mm | No | Yes | No | 350 mm  [stored 1.14829 ft] | 210 mm  [stored 0.688976 ft] | 140 mm  [stored 0.459318 ft] | Thorn-Aluminium-RAL 9016-Traffic White | 96701226 | TLG_CESA_F_AMP_DWN_WB_WH.jpg | Thorn-Light Source-Cesar-Amp-Wall : CESAR AMP M DWN 1L940MB RD WH_photometric_data | Thorn-Light Source-Cesar-Amp-Wall : CESAR AMP M DWN 1L940MB RD WH_photometric_data | No | 19 W |
| CESAR AMP M U/D 2L927MB HF ANT | 37 VA | 70 mm  [stored 0.229659 ft] | 17 mm | No | Yes | No | 350 mm  [stored 1.14829 ft] | 210 mm  [stored 0.688976 ft] | 140 mm  [stored 0.459318 ft] | Thorn-Aluminium-RAL 7016-Anthracite Grey | 96700085 | TLG_CESA_F_AMP_UD_WB_ANT.jpg | Thorn-Light Source-Cesar-Amp-Wall : CESAR AMP M U/D 2L927MB HF ANT_photometric_data_DOWN | Thorn-Light Source-Cesar-Amp-Wall : CESAR AMP M U/D 2L927MB HF ANT_photometric_data_UP | Yes | 37 W |
| CESAR AMP M U/D 2L927MB HF BK | 37 VA | 70 mm  [stored 0.229659 ft] | 17 mm | No | Yes | No | 350 mm  [stored 1.14829 ft] | 210 mm  [stored 0.688976 ft] | 140 mm  [stored 0.459318 ft] | Thorn-Aluminium-RAL 9005-Jet Black | 96700083 | TLG_CESA_F_AMP_UD_WB_BK.jpg | Thorn-Light Source-Cesar-Amp-Wall : CESAR AMP M U/D 2L927MB HF BK_photometric_data_DOWN | Thorn-Light Source-Cesar-Amp-Wall : CESAR AMP M U/D 2L927MB HF BK_photometric_data_UP | Yes | 37 W |
| CESAR AMP M U/D 2L927MB HF GY | 37 VA | 70 mm  [stored 0.229659 ft] | 17 mm | No | Yes | No | 350 mm  [stored 1.14829 ft] | 210 mm  [stored 0.688976 ft] | 140 mm  [stored 0.459318 ft] | Thorn-Aluminium-RAL 9006-White Aluminium | 96700084 | TLG_CESA_F_AMP_UD_WB_GY.jpg | Thorn-Light Source-Cesar-Amp-Wall : CESAR AMP M U/D 2L927MB HF GY_photometric_data_DOWN | Thorn-Light Source-Cesar-Amp-Wall : CESAR AMP M U/D 2L927MB HF GY_photometric_data_UP | Yes | 37 W |
| CESAR AMP M U/D 2L927MB HF WH | 37 VA | 70 mm  [stored 0.229659 ft] | 17 mm | No | Yes | No | 350 mm  [stored 1.14829 ft] | 210 mm  [stored 0.688976 ft] | 140 mm  [stored 0.459318 ft] | Thorn-Aluminium-RAL 9016-Traffic White | 96700082 | TLG_CESA_F_AMP_UD_WB_WH.jpg | Thorn-Light Source-Cesar-Amp-Wall : CESAR AMP M U/D 2L927MB HF WH_photometric_data_DOWN | Thorn-Light Source-Cesar-Amp-Wall : CESAR AMP M U/D 2L927MB HF WH_photometric_data_UP | Yes | 37 W |
| CESAR AMP M U/D 2L927MB RD ANT | 37 VA | 70 mm  [stored 0.229659 ft] | 17 mm | No | Yes | No | 350 mm  [stored 1.14829 ft] | 210 mm  [stored 0.688976 ft] | 140 mm  [stored 0.459318 ft] | Thorn-Aluminium-RAL 7016-Anthracite Grey | 96701237 | TLG_CESA_F_AMP_UD_WB_ANT.jpg | Thorn-Light Source-Cesar-Amp-Wall : CESAR AMP M U/D 2L927MB RD ANT_photometric_data_DOWN | Thorn-Light Source-Cesar-Amp-Wall : CESAR AMP M U/D 2L927MB RD ANT_photometric_data_UP | Yes | 37 W |
| CESAR AMP M U/D 2L927MB RD BK | 37 VA | 70 mm  [stored 0.229659 ft] | 17 mm | No | Yes | No | 350 mm  [stored 1.14829 ft] | 210 mm  [stored 0.688976 ft] | 140 mm  [stored 0.459318 ft] | Thorn-Aluminium-RAL 9005-Jet Black | 96701235 | TLG_CESA_F_AMP_UD_WB_BK.jpg | Thorn-Light Source-Cesar-Amp-Wall : CESAR AMP M U/D 2L927MB RD BK_photometric_data_DOWN | Thorn-Light Source-Cesar-Amp-Wall : CESAR AMP M U/D 2L927MB RD BK_photometric_data_UP | Yes | 37 W |
| CESAR AMP M U/D 2L927MB RD GY | 37 VA | 70 mm  [stored 0.229659 ft] | 17 mm | No | Yes | No | 350 mm  [stored 1.14829 ft] | 210 mm  [stored 0.688976 ft] | 140 mm  [stored 0.459318 ft] | Thorn-Aluminium-RAL 9006-White Aluminium | 96701236 | TLG_CESA_F_AMP_UD_WB_GY.jpg | Thorn-Light Source-Cesar-Amp-Wall : CESAR AMP M U/D 2L927MB RD GY_photometric_data_DOWN | Thorn-Light Source-Cesar-Amp-Wall : CESAR AMP M U/D 2L927MB RD GY_photometric_data_UP | Yes | 37 W |
| CESAR AMP M U/D 2L927MB RD WH | 37 VA | 70 mm  [stored 0.229659 ft] | 17 mm | No | Yes | No | 350 mm  [stored 1.14829 ft] | 210 mm  [stored 0.688976 ft] | 140 mm  [stored 0.459318 ft] | Thorn-Aluminium-RAL 9016-Traffic White | 96701234 | TLG_CESA_F_AMP_UD_WB_WH.jpg | Thorn-Light Source-Cesar-Amp-Wall : CESAR AMP M U/D 2L927MB RD WH_photometric_data_DOWN | Thorn-Light Source-Cesar-Amp-Wall : CESAR AMP M U/D 2L927MB RD WH_photometric_data_UP | Yes | 37 W |
| CESAR AMP M U/D 2L930MB HF ANT | 37 VA | 70 mm  [stored 0.229659 ft] | 17 mm | No | Yes | No | 350 mm  [stored 1.14829 ft] | 210 mm  [stored 0.688976 ft] | 140 mm  [stored 0.459318 ft] | Thorn-Aluminium-RAL 7016-Anthracite Grey | 96700093 | TLG_CESA_F_AMP_UD_WB_ANT.jpg | Thorn-Light Source-Cesar-Amp-Wall : CESAR AMP M U/D 2L930MB HF ANT_photometric_data_DOWN | Thorn-Light Source-Cesar-Amp-Wall : CESAR AMP M U/D 2L930MB HF ANT_photometric_data_UP | Yes | 37 W |
| CESAR AMP M U/D 2L930MB HF BK | 37 VA | 70 mm  [stored 0.229659 ft] | 17 mm | No | Yes | No | 350 mm  [stored 1.14829 ft] | 210 mm  [stored 0.688976 ft] | 140 mm  [stored 0.459318 ft] | Thorn-Aluminium-RAL 9005-Jet Black | 96700091 | TLG_CESA_F_AMP_UD_WB_BK.jpg | Thorn-Light Source-Cesar-Amp-Wall : CESAR AMP M U/D 2L930MB HF BK_photometric_data_DOWN | Thorn-Light Source-Cesar-Amp-Wall : CESAR AMP M U/D 2L930MB HF BK_photometric_data_UP | Yes | 37 W |
| CESAR AMP M U/D 2L930MB HF GY | 37 VA | 70 mm  [stored 0.229659 ft] | 17 mm | No | Yes | No | 350 mm  [stored 1.14829 ft] | 210 mm  [stored 0.688976 ft] | 140 mm  [stored 0.459318 ft] | Thorn-Aluminium-RAL 9006-White Aluminium | 96700092 | TLG_CESA_F_AMP_UD_WB_GY.jpg | Thorn-Light Source-Cesar-Amp-Wall : CESAR AMP M U/D 2L930MB HF GY_photometric_data_DOWN | Thorn-Light Source-Cesar-Amp-Wall : CESAR AMP M U/D 2L930MB HF GY_photometric_data_UP | Yes | 37 W |
| CESAR AMP M U/D 2L930MB HF WH | 37 VA | 70 mm  [stored 0.229659 ft] | 17 mm | No | Yes | No | 350 mm  [stored 1.14829 ft] | 210 mm  [stored 0.688976 ft] | 140 mm  [stored 0.459318 ft] | Thorn-Aluminium-RAL 9016-Traffic White | 96700090 | TLG_CESA_F_AMP_UD_WB_WH.jpg | Thorn-Light Source-Cesar-Amp-Wall : CESAR AMP M U/D 2L930MB HF WH_photometric_data_DOWN | Thorn-Light Source-Cesar-Amp-Wall : CESAR AMP M U/D 2L930MB HF WH_photometric_data_UP | Yes | 37 W |
| CESAR AMP M U/D 2L930MB RD ANT | 37 VA | 70 mm  [stored 0.229659 ft] | 17 mm | No | Yes | No | 350 mm  [stored 1.14829 ft] | 210 mm  [stored 0.688976 ft] | 140 mm  [stored 0.459318 ft] | Thorn-Aluminium-RAL 7016-Anthracite Grey | 96701245 | TLG_CESA_F_AMP_UD_WB_ANT.jpg | Thorn-Light Source-Cesar-Amp-Wall : CESAR AMP M U/D 2L930MB RD ANT_photometric_data_DOWN | Thorn-Light Source-Cesar-Amp-Wall : CESAR AMP M U/D 2L930MB RD ANT_photometric_data_UP | Yes | 37 W |
| CESAR AMP M U/D 2L930MB RD BK | 37 VA | 70 mm  [stored 0.229659 ft] | 17 mm | No | Yes | No | 350 mm  [stored 1.14829 ft] | 210 mm  [stored 0.688976 ft] | 140 mm  [stored 0.459318 ft] | Thorn-Aluminium-RAL 9005-Jet Black | 96701243 | TLG_CESA_F_AMP_UD_WB_BK.jpg | Thorn-Light Source-Cesar-Amp-Wall : CESAR AMP M U/D 2L930MB RD BK_photometric_data_DOWN | Thorn-Light Source-Cesar-Amp-Wall : CESAR AMP M U/D 2L930MB RD BK_photometric_data_UP | Yes | 37 W |
| CESAR AMP M U/D 2L930MB RD GY | 37 VA | 70 mm  [stored 0.229659 ft] | 17 mm | No | Yes | No | 350 mm  [stored 1.14829 ft] | 210 mm  [stored 0.688976 ft] | 140 mm  [stored 0.459318 ft] | Thorn-Aluminium-RAL 9006-White Aluminium | 96701244 | TLG_CESA_F_AMP_UD_WB_GY.jpg | Thorn-Light Source-Cesar-Amp-Wall : CESAR AMP M U/D 2L930MB RD GY_photometric_data_DOWN | Thorn-Light Source-Cesar-Amp-Wall : CESAR AMP M U/D 2L930MB RD GY_photometric_data_UP | Yes | 37 W |
| CESAR AMP M U/D 2L930MB RD WH | 37 VA | 70 mm  [stored 0.229659 ft] | 17 mm | No | Yes | No | 350 mm  [stored 1.14829 ft] | 210 mm  [stored 0.688976 ft] | 140 mm  [stored 0.459318 ft] | Thorn-Aluminium-RAL 9016-Traffic White | 96701242 | TLG_CESA_F_AMP_UD_WB_WH.jpg | Thorn-Light Source-Cesar-Amp-Wall : CESAR AMP M U/D 2L930MB RD WH_photometric_data_DOWN | Thorn-Light Source-Cesar-Amp-Wall : CESAR AMP M U/D 2L930MB RD WH_photometric_data_UP | Yes | 37 W |
| CESAR AMP M U/D 2L940MB HF ANT | 37 VA | 70 mm  [stored 0.229659 ft] | 17 mm | No | Yes | No | 350 mm  [stored 1.14829 ft] | 210 mm  [stored 0.688976 ft] | 140 mm  [stored 0.459318 ft] | Thorn-Aluminium-RAL 7016-Anthracite Grey | 96700089 | TLG_CESA_F_AMP_UD_WB_ANT.jpg | Thorn-Light Source-Cesar-Amp-Wall : CESAR AMP M U/D 2L940MB HF ANT_photometric_data_DOWN | Thorn-Light Source-Cesar-Amp-Wall : CESAR AMP M U/D 2L940MB HF ANT_photometric_data_UP | Yes | 37 W |
| CESAR AMP M U/D 2L940MB HF BK | 37 VA | 70 mm  [stored 0.229659 ft] | 17 mm | No | Yes | No | 350 mm  [stored 1.14829 ft] | 210 mm  [stored 0.688976 ft] | 140 mm  [stored 0.459318 ft] | Thorn-Aluminium-RAL 9005-Jet Black | 96700087 | TLG_CESA_F_AMP_UD_WB_BK.jpg | Thorn-Light Source-Cesar-Amp-Wall : CESAR AMP M U/D 2L940MB HF BK_photometric_data_DOWN | Thorn-Light Source-Cesar-Amp-Wall : CESAR AMP M U/D 2L940MB HF BK_photometric_data_UP | Yes | 37 W |
| CESAR AMP M U/D 2L940MB HF GY | 37 VA | 70 mm  [stored 0.229659 ft] | 17 mm | No | Yes | No | 350 mm  [stored 1.14829 ft] | 210 mm  [stored 0.688976 ft] | 140 mm  [stored 0.459318 ft] | Thorn-Aluminium-RAL 9006-White Aluminium | 96700088 | TLG_CESA_F_AMP_UD_WB_GY.jpg | Thorn-Light Source-Cesar-Amp-Wall : CESAR AMP M U/D 2L940MB HF GY_photometric_data_DOWN | Thorn-Light Source-Cesar-Amp-Wall : CESAR AMP M U/D 2L940MB HF GY_photometric_data_UP | Yes | 37 W |
| CESAR AMP M U/D 2L940MB HF WH | 37 VA | 70 mm  [stored 0.229659 ft] | 17 mm | No | Yes | No | 350 mm  [stored 1.14829 ft] | 210 mm  [stored 0.688976 ft] | 140 mm  [stored 0.459318 ft] | Thorn-Aluminium-RAL 9016-Traffic White | 96700086 | TLG_CESA_F_AMP_UD_WB_WH.jpg | Thorn-Light Source-Cesar-Amp-Wall : CESAR AMP M U/D 2L940MB HF WH_photometric_data_DOWN | Thorn-Light Source-Cesar-Amp-Wall : CESAR AMP M U/D 2L940MB HF WH_photometric_data_UP | Yes | 37 W |
| CESAR AMP M U/D 2L940MB RD ANT | 37 VA | 70 mm  [stored 0.229659 ft] | 17 mm | No | Yes | No | 350 mm  [stored 1.14829 ft] | 210 mm  [stored 0.688976 ft] | 140 mm  [stored 0.459318 ft] | Thorn-Aluminium-RAL 7016-Anthracite Grey | 96701241 | TLG_CESA_F_AMP_UD_WB_ANT.jpg | Thorn-Light Source-Cesar-Amp-Wall : CESAR AMP M U/D 2L940MB RD ANT_photometric_data_DOWN | Thorn-Light Source-Cesar-Amp-Wall : CESAR AMP M U/D 2L940MB RD ANT_photometric_data_UP | Yes | 37 W |
| CESAR AMP M U/D 2L940MB RD BK | 37 VA | 70 mm  [stored 0.229659 ft] | 17 mm | No | Yes | No | 350 mm  [stored 1.14829 ft] | 210 mm  [stored 0.688976 ft] | 140 mm  [stored 0.459318 ft] | Thorn-Aluminium-RAL 9005-Jet Black | 96701239 | TLG_CESA_F_AMP_UD_WB_BK.jpg | Thorn-Light Source-Cesar-Amp-Wall : CESAR AMP M U/D 2L940MB RD BK_photometric_data_DOWN | Thorn-Light Source-Cesar-Amp-Wall : CESAR AMP M U/D 2L940MB RD BK_photometric_data_UP | Yes | 37 W |
| CESAR AMP M U/D 2L940MB RD GY | 37 VA | 70 mm  [stored 0.229659 ft] | 17 mm | No | Yes | No | 350 mm  [stored 1.14829 ft] | 210 mm  [stored 0.688976 ft] | 140 mm  [stored 0.459318 ft] | Thorn-Aluminium-RAL 9006-White Aluminium | 96701240 | TLG_CESA_F_AMP_UD_WB_GY.jpg | Thorn-Light Source-Cesar-Amp-Wall : CESAR AMP M U/D 2L940MB RD GY_photometric_data_DOWN | Thorn-Light Source-Cesar-Amp-Wall : CESAR AMP M U/D 2L940MB RD GY_photometric_data_UP | Yes | 37 W |
| CESAR AMP M U/D 2L940MB RD WH | 37 VA | 70 mm  [stored 0.229659 ft] | 17 mm | No | Yes | No | 350 mm  [stored 1.14829 ft] | 210 mm  [stored 0.688976 ft] | 140 mm  [stored 0.459318 ft] | Thorn-Aluminium-RAL 9016-Traffic White | 96701238 | TLG_CESA_F_AMP_UD_WB_WH.jpg | Thorn-Light Source-Cesar-Amp-Wall : CESAR AMP M U/D 2L940MB RD WH_photometric_data_DOWN | Thorn-Light Source-Cesar-Amp-Wall : CESAR AMP M U/D 2L940MB RD WH_photometric_data_UP | Yes | 37 W |
| CESAR AMP L DWN 1L927MB HFX BK | 34 VA | 100 mm  [stored 0.328084 ft] | 22 mm  [stored 0.0721785 ft] | Yes | No | No | 450 mm  [stored 1.47638 ft] | 275 mm | 200 mm  [stored 0.656168 ft] | Thorn-Aluminium-RAL 9005-Jet Black | 96700107 | TLG_CESA_F_AMP_DWN_WB_BK.jpg | Thorn-Light Source-Cesar-Amp-Wall : CESAR AMP L DWN 1L927MB HFX BK_photometric_data | Thorn-Light Source-Cesar-Amp-Wall : CESAR AMP L DWN 1L927MB HFX BK_photometric_data | No | 34 W |
| CESAR AMP L DWN 1L927MB HFX WH | 34 VA | 100 mm  [stored 0.328084 ft] | 22 mm  [stored 0.0721785 ft] | Yes | No | No | 450 mm  [stored 1.47638 ft] | 275 mm | 200 mm  [stored 0.656168 ft] | Thorn-Aluminium-RAL 9016-Traffic White | 96700106 | TLG_CESA_F_AMP_DWN_WB_WH.jpg | Thorn-Light Source-Cesar-Amp-Wall : CESAR AMP L DWN 1L927MB HFX WH_photometric_data | Thorn-Light Source-Cesar-Amp-Wall : CESAR AMP L DWN 1L927MB HFX WH_photometric_data | No | 34 W |
| CESAR AMP L DWN 1L927MBHFX ANT | 34 VA | 100 mm  [stored 0.328084 ft] | 22 mm  [stored 0.0721785 ft] | Yes | No | No | 450 mm  [stored 1.47638 ft] | 275 mm | 200 mm  [stored 0.656168 ft] | Thorn-Aluminium-RAL 7016-Anthracite Grey | 96700109 | TLG_CESA_F_AMP_DWN_WB_ANT.jpg | Thorn-Light Source-Cesar-Amp-Wall : CESAR AMP L DWN 1L927MBHFX ANT_photometric_data | Thorn-Light Source-Cesar-Amp-Wall : CESAR AMP L DWN 1L927MBHFX ANT_photometric_data | No | 34 W |
| CESAR AMP L DWN 1L927MBHFX GY | 34 VA | 100 mm  [stored 0.328084 ft] | 22 mm  [stored 0.0721785 ft] | Yes | No | No | 450 mm  [stored 1.47638 ft] | 275 mm | 200 mm  [stored 0.656168 ft] | Thorn-Aluminium-RAL 9006-White Aluminium | 96700108 | TLG_CESA_F_AMP_DWN_WB_GY.jpg | Thorn-Light Source-Cesar-Amp-Wall : CESAR AMP L DWN 1L927MBHFX GY_photometric_data | Thorn-Light Source-Cesar-Amp-Wall : CESAR AMP L DWN 1L927MBHFX GY_photometric_data | No | 34 W |
| CESAR AMP L DWN 1L930MBHFX ANT | 34 VA | 100 mm  [stored 0.328084 ft] | 22 mm  [stored 0.0721785 ft] | Yes | No | No | 450 mm  [stored 1.47638 ft] | 275 mm | 200 mm  [stored 0.656168 ft] | Thorn-Aluminium-RAL 7016-Anthracite Grey | 96700117 | TLG_CESA_F_AMP_DWN_WB_ANT.jpg | Thorn-Light Source-Cesar-Amp-Wall : CESAR AMP L DWN 1L930MBHFX ANT_photometric_data | Thorn-Light Source-Cesar-Amp-Wall : CESAR AMP L DWN 1L930MBHFX ANT_photometric_data | No | 34 W |
| CESAR AMP L DWN 1L930MBHFX BK | 34 VA | 100 mm  [stored 0.328084 ft] | 22 mm  [stored 0.0721785 ft] | Yes | No | No | 450 mm  [stored 1.47638 ft] | 275 mm | 200 mm  [stored 0.656168 ft] | Thorn-Aluminium-RAL 9005-Jet Black | 96700115 | TLG_CESA_F_AMP_DWN_WB_BK.jpg | Thorn-Light Source-Cesar-Amp-Wall : CESAR AMP L DWN 1L930MBHFX BK_photometric_data | Thorn-Light Source-Cesar-Amp-Wall : CESAR AMP L DWN 1L930MBHFX BK_photometric_data | No | 34 W |
| CESAR AMP L DWN 1L930MBHFX GY | 34 VA | 100 mm  [stored 0.328084 ft] | 22 mm  [stored 0.0721785 ft] | Yes | No | No | 450 mm  [stored 1.47638 ft] | 275 mm | 200 mm  [stored 0.656168 ft] | Thorn-Aluminium-RAL 9006-White Aluminium | 96700116 | TLG_CESA_F_AMP_DWN_WB_GY.jpg | Thorn-Light Source-Cesar-Amp-Wall : CESAR AMP L DWN 1L930MBHFX GY_photometric_data | Thorn-Light Source-Cesar-Amp-Wall : CESAR AMP L DWN 1L930MBHFX GY_photometric_data | No | 34 W |
| CESAR AMP L DWN 1L930MBHFX WH | 34 VA | 100 mm  [stored 0.328084 ft] | 22 mm  [stored 0.0721785 ft] | Yes | No | No | 450 mm  [stored 1.47638 ft] | 275 mm | 200 mm  [stored 0.656168 ft] | Thorn-Aluminium-RAL 9016-Traffic White | 96700114 | TLG_CESA_F_AMP_DWN_WB_WH.jpg | Thorn-Light Source-Cesar-Amp-Wall : CESAR AMP L DWN 1L930MBHFX WH_photometric_data | Thorn-Light Source-Cesar-Amp-Wall : CESAR AMP L DWN 1L930MBHFX WH_photometric_data | No | 34 W |
| CESAR AMP L DWN 1L940MBHFX ANT | 34 VA | 100 mm  [stored 0.328084 ft] | 22 mm  [stored 0.0721785 ft] | Yes | No | No | 450 mm  [stored 1.47638 ft] | 275 mm | 200 mm  [stored 0.656168 ft] | Thorn-Aluminium-RAL 7016-Anthracite Grey | 96700113 | TLG_CESA_F_AMP_DWN_WB_ANT.jpg | Thorn-Light Source-Cesar-Amp-Wall : CESAR AMP L DWN 1L940MBHFX ANT_photometric_data | Thorn-Light Source-Cesar-Amp-Wall : CESAR AMP L DWN 1L940MBHFX ANT_photometric_data | No | 34 W |
| CESAR AMP L DWN 1L940MBHFX BK | 34 VA | 100 mm  [stored 0.328084 ft] | 22 mm  [stored 0.0721785 ft] | Yes | No | No | 450 mm  [stored 1.47638 ft] | 275 mm | 200 mm  [stored 0.656168 ft] | Thorn-Aluminium-RAL 9005-Jet Black | 96700111 | TLG_CESA_F_AMP_DWN_WB_BK.jpg | Thorn-Light Source-Cesar-Amp-Wall : CESAR AMP L DWN 1L940MBHFX BK_photometric_data | Thorn-Light Source-Cesar-Amp-Wall : CESAR AMP L DWN 1L940MBHFX BK_photometric_data | No | 34 W |
| CESAR AMP L DWN 1L940MBHFX GY | 34 VA | 100 mm  [stored 0.328084 ft] | 22 mm  [stored 0.0721785 ft] | Yes | No | No | 450 mm  [stored 1.47638 ft] | 275 mm | 200 mm  [stored 0.656168 ft] | Thorn-Aluminium-RAL 9006-White Aluminium | 96700112 | TLG_CESA_F_AMP_DWN_WB_GY.jpg | Thorn-Light Source-Cesar-Amp-Wall : CESAR AMP L DWN 1L940MBHFX GY_photometric_data | Thorn-Light Source-Cesar-Amp-Wall : CESAR AMP L DWN 1L940MBHFX GY_photometric_data | No | 34 W |
| CESAR AMP L DWN 1L940MBHFX WH | 34 VA | 100 mm  [stored 0.328084 ft] | 22 mm  [stored 0.0721785 ft] | Yes | No | No | 450 mm  [stored 1.47638 ft] | 275 mm | 200 mm  [stored 0.656168 ft] | Thorn-Aluminium-RAL 9016-Traffic White | 96700110 | TLG_CESA_F_AMP_DWN_WB_WH.jpg | Thorn-Light Source-Cesar-Amp-Wall : CESAR AMP L DWN 1L940MBHFX WH_photometric_data | Thorn-Light Source-Cesar-Amp-Wall : CESAR AMP L DWN 1L940MBHFX WH_photometric_data | No | 34 W |
| CESAR AMP L U/D 2L927FM HFX ANT | 69 VA | 100 mm  [stored 0.328084 ft] | 22 mm  [stored 0.0721785 ft] | Yes | No | No | 450 mm  [stored 1.47638 ft] | 275 mm | 200 mm  [stored 0.656168 ft] | Thorn-Aluminium-RAL 7016-Anthracite Grey | 96700121 | TLG_CESA_F_AMP_UD_WB_ANT.jpg | Thorn-Light Source-Cesar-Amp-Wall : CESAR AMP L U/D 2L927FM HFX ANT_photometric_data_DOWN | Thorn-Light Source-Cesar-Amp-Wall : CESAR AMP L U/D 2L927FM HFX ANT_photometric_data_UP | Yes | 69 W |
| CESAR AMP L U/D 2L927FM HFX BK | 69 VA | 100 mm  [stored 0.328084 ft] | 22 mm  [stored 0.0721785 ft] | Yes | No | No | 450 mm  [stored 1.47638 ft] | 275 mm | 200 mm  [stored 0.656168 ft] | Thorn-Aluminium-RAL 9005-Jet Black | 96700119 | TLG_CESA_F_AMP_UD_WB_BK.jpg | Thorn-Light Source-Cesar-Amp-Wall : CESAR AMP L U/D 2L927FM HFX BK_photometric_data_DOWN | Thorn-Light Source-Cesar-Amp-Wall : CESAR AMP L U/D 2L927FM HFX BK_photometric_data_UP | Yes | 69 W |
| CESAR AMP L U/D 2L927FM HFX GY | 69 VA | 100 mm  [stored 0.328084 ft] | 22 mm  [stored 0.0721785 ft] | Yes | No | No | 450 mm  [stored 1.47638 ft] | 275 mm | 200 mm  [stored 0.656168 ft] | Thorn-Aluminium-RAL 9006-White Aluminium | 96700120 | TLG_CESA_F_AMP_UD_WB_GY.jpg | Thorn-Light Source-Cesar-Amp-Wall : CESAR AMP L U/D 2L927FM HFX GY_photometric_data_DOWN | Thorn-Light Source-Cesar-Amp-Wall : CESAR AMP L U/D 2L927FM HFX GY_photometric_data_UP | Yes | 69 W |
| CESAR AMP L U/D 2L927FM HFX WH | 69 VA | 100 mm  [stored 0.328084 ft] | 22 mm  [stored 0.0721785 ft] | Yes | No | No | 450 mm  [stored 1.47638 ft] | 275 mm | 200 mm  [stored 0.656168 ft] | Thorn-Aluminium-RAL 9016-Traffic White | 96700118 | TLG_CESA_F_AMP_CEI_WB_ANT.jpg | Thorn-Light Source-Cesar-Amp-Wall : CESAR AMP L U/D 2L927FM HFX WH_photometric_data_DOWN | Thorn-Light Source-Cesar-Amp-Wall : CESAR AMP L U/D 2L927FM HFX WH_photometric_data_UP | Yes | 69 W |
| CESAR AMP L U/D 2L930FM HFX ANT | 69 VA | 100 mm  [stored 0.328084 ft] | 22 mm  [stored 0.0721785 ft] | Yes | No | No | 450 mm  [stored 1.47638 ft] | 275 mm | 200 mm  [stored 0.656168 ft] | Thorn-Aluminium-RAL 7016-Anthracite Grey | 96700129 | TLG_CESA_F_AMP_UD_WB_ANT.jpg | Thorn-Light Source-Cesar-Amp-Wall : CESAR AMP L U/D 2L930FM HFX ANT_photometric_data_DOWN | Thorn-Light Source-Cesar-Amp-Wall : CESAR AMP L U/D 2L930FM HFX ANT_photometric_data_UP | Yes | 69 W |
| CESAR AMP L U/D 2L930FM HFX BK | 69 VA | 100 mm  [stored 0.328084 ft] | 22 mm  [stored 0.0721785 ft] | Yes | No | No | 450 mm  [stored 1.47638 ft] | 275 mm | 200 mm  [stored 0.656168 ft] | Thorn-Aluminium-RAL 9005-Jet Black | 96700127 | TLG_CESA_F_AMP_UD_WB_BK.jpg | Thorn-Light Source-Cesar-Amp-Wall : CESAR AMP L U/D 2L930FM HFX BK_photometric_data_DOWN | Thorn-Light Source-Cesar-Amp-Wall : CESAR AMP L U/D 2L930FM HFX BK_photometric_data_UP | Yes | 69 W |
| CESAR AMP L U/D 2L930FM HFX GY | 69 VA | 100 mm  [stored 0.328084 ft] | 22 mm  [stored 0.0721785 ft] | Yes | No | No | 450 mm  [stored 1.47638 ft] | 275 mm | 200 mm  [stored 0.656168 ft] | Thorn-Aluminium-RAL 9006-White Aluminium | 96700128 | TLG_CESA_F_AMP_UD_WB_GY.jpg | Thorn-Light Source-Cesar-Amp-Wall : CESAR AMP L U/D 2L930FM HFX GY_photometric_data_DOWN | Thorn-Light Source-Cesar-Amp-Wall : CESAR AMP L U/D 2L930FM HFX GY_photometric_data_UP | Yes | 69 W |
| CESAR AMP L U/D 2L930FM HFX WH | 69 VA | 100 mm  [stored 0.328084 ft] | 22 mm  [stored 0.0721785 ft] | Yes | No | No | 450 mm  [stored 1.47638 ft] | 275 mm | 200 mm  [stored 0.656168 ft] | Thorn-Aluminium-RAL 9016-Traffic White | 96700126 | TLG_CESA_F_AMP_UD_WB_WH.jpg | Thorn-Light Source-Cesar-Amp-Wall : CESAR AMP L U/D 2L930FM HFX WH_photometric_data_DOWN | Thorn-Light Source-Cesar-Amp-Wall : CESAR AMP L U/D 2L930FM HFX WH_photometric_data_UP | Yes | 69 W |
| CESAR AMP L U/D 2L940FM HFX ANT | 69 VA | 100 mm  [stored 0.328084 ft] | 22 mm  [stored 0.0721785 ft] | Yes | No | No | 450 mm  [stored 1.47638 ft] | 275 mm | 200 mm  [stored 0.656168 ft] | Thorn-Aluminium-RAL 7016-Anthracite Grey | 96700125 | TLG_CESA_F_AMP_UD_WB_ANT.jpg | Thorn-Light Source-Cesar-Amp-Wall : CESAR AMP L U/D 2L940FM HFX ANT_photometric_data_DOWN | Thorn-Light Source-Cesar-Amp-Wall : CESAR AMP L U/D 2L940FM HFX ANT_photometric_data_UP | Yes | 69 W |
| CESAR AMP L U/D 2L940FM HFX BK | 69 VA | 100 mm  [stored 0.328084 ft] | 22 mm  [stored 0.0721785 ft] | Yes | No | No | 450 mm  [stored 1.47638 ft] | 275 mm | 200 mm  [stored 0.656168 ft] | Thorn-Aluminium-RAL 9005-Jet Black | 96700123 | TLG_CESA_F_AMP_UD_WB_BK.jpg | Thorn-Light Source-Cesar-Amp-Wall : CESAR AMP L U/D 2L940FM HFX BK_photometric_data_DOWN | Thorn-Light Source-Cesar-Amp-Wall : CESAR AMP L U/D 2L940FM HFX BK_photometric_data_UP | Yes | 69 W |
| CESAR AMP L U/D 2L940FM HFX GY | 69 VA | 100 mm  [stored 0.328084 ft] | 22 mm  [stored 0.0721785 ft] | Yes | No | No | 450 mm  [stored 1.47638 ft] | 275 mm | 200 mm  [stored 0.656168 ft] | Thorn-Aluminium-RAL 9006-White Aluminium | 96700124 | TLG_CESA_F_AMP_UD_WB_GY.jpg | Thorn-Light Source-Cesar-Amp-Wall : CESAR AMP L U/D 2L940FM HFX GY_photometric_data_DOWN | Thorn-Light Source-Cesar-Amp-Wall : CESAR AMP L U/D 2L940FM HFX GY_photometric_data_UP | Yes | 69 W |
| CESAR AMP L U/D 2L940FM HFX WH | 69 VA | 100 mm  [stored 0.328084 ft] | 22 mm  [stored 0.0721785 ft] | Yes | No | No | 450 mm  [stored 1.47638 ft] | 275 mm | 200 mm  [stored 0.656168 ft] | Thorn-Aluminium-RAL 9016-Traffic White | 96700122 | TLG_CESA_F_AMP_UD_WB_WH.jpg | Thorn-Light Source-Cesar-Amp-Wall : CESAR AMP L U/D 2L940FM HFX WH_photometric_data_DOWN | Thorn-Light Source-Cesar-Amp-Wall : CESAR AMP L U/D 2L940FM HFX WH_photometric_data_UP | Yes | 69 W |

note: [stored X ft] marks values corroborated as IEEE doubles in the binary element streams (Revit-internal decimal feet)

## geometry (parser evidence)
native form markers: Sweep x6
no freeform markers — native parametric forms only
